# Revit family: BTicino-Hotel_UX_ONE-Thermostat
name_source: partatom
category: Equipement électrique
units: mm (PartAtom-declared; Revit-internal decimal feet)

## family parameters
Configuration du panneau = Deux colonnes, circuits au sein
Cote de connecteur circulaire = Utiliser le diamètre
Couper avec des vides une fois chargée = Non
Hôte = Face
Partagée = Non
Point de calcul de pièce = Non
Type d'élément = Tableau de raccordement

## types (8) — shared parameters
Avec affichage = Oui
Conditions Générale d'Utilisation = https://export.legrand.com
Ecran Tactile = Oui
Elévation par défaut = 1500 mm  [stored 4.92126 ft]
Fabricant = BTICINO
Fonction ne pas Déranger = Non
Fonctionnement en parallèle possible = Oui
Hauteur = 93 mm  [stored 0.305118 ft]
IK = 04
IP = 20
Largeur = 129 mm  [stored 0.423228 ft]
Matière = Plastique
Réglage manuel de la valeur de consigne = Oui
Site web configurateur = https://uxforhotels.legrand.com
Système de bus radio = Oui
profondeur d'encastrement = 50 mm  [stored 0.164042 ft]

## per-type parameters (varying)
| type | Couleur | Désignation produit | Hauteur pictogrammes | Hauteur vide | Matériau plaque | Matériau écran | Mode de pose | Plaque apparente | Plaque encastrée | Profondeur | Référence / Modèle | Tension |
| Noir 230V Encastré | Noir | HOTEL THERMOSTAT  ENCASTRE NOIR 230V | 0 mm  [stored 0 ft] | -40 mm  [stored -0.131234 ft] | LEGRAND_BLACK_PLASTIC | LEGRAND_BLACK_SCREEN | Encastré | Non | Oui | 52 mm | BT-465001 | 230 V AC |
| Noir 230V Apparent | Noir | HOTEL THERMOSTAT  SAILLIE NOIR 230V | 16 mm | 0 mm  [stored 0 ft] | LEGRAND_BLACK_PLASTIC | LEGRAND_BLACK_SCREEN | saillie | Oui | Non | 28 mm  [stored 0.0918635 ft] | BT-465002 | 230 V AC |
| Blanc 230V Encastré | Blanc | HOTEL THERMOSTAT  ENCASTRE BLANC 230V | 0 mm  [stored 0 ft] | -40 mm  [stored -0.131234 ft] | LEGRAND_WHITE_PLASTIC | LEGRAND_WHITE_SCREEN | Encastré | Non | Oui | 52 mm | BT-465003 | 230 V AC |
| Blanc 230V Apparent | Blanc | HOTEL THERMOSTAT  SAILLIE BLANC 230V | 16 mm | 0 mm  [stored 0 ft] | LEGRAND_WHITE_PLASTIC | LEGRAND_WHITE_SCREEN | saillie | Oui | Non | 28 mm  [stored 0.0918635 ft] | BT-465004 | 230 V AC |
| Noir 24V Encastré | Noir | HOTEL THERMOSTAT  ENCASTRE NOIR 24V | 0 mm  [stored 0 ft] | -40 mm  [stored -0.131234 ft] | LEGRAND_BLACK_PLASTIC | LEGRAND_BLACK_SCREEN | Encastré | Non | Oui | 52 mm | BT-465005 | 24 V |
| Noir 24V Apparent | Noir | HOTEL THERMOSTAT  SAILLIE NOIR 24V | 16 mm | 0 mm  [stored 0 ft] | LEGRAND_BLACK_PLASTIC | LEGRAND_BLACK_SCREEN | saillie | Oui | Non | 28 mm  [stored 0.0918635 ft] | BT-465006 | 24 V |
| Blanc 24V Encastré | Blanc | HOTEL THERMOSTAT ENCASTRE BLANC 24V | 0 mm  [stored 0 ft] | -40 mm  [stored -0.131234 ft] | LEGRAND_WHITE_PLASTIC | LEGRAND_WHITE_SCREEN | Encastré | Non | Oui | 52 mm | BT-465007 | 24 V |
| Blanc 24V Apparent | Blanc | HOTEL THERMOSTAT  SAILLIE BLANC 24V | 16 mm | 0 mm  [stored 0 ft] | LEGRAND_WHITE_PLASTIC | LEGRAND_WHITE_SCREEN | saillie | Oui | Non | 28 mm  [stored 0.0918635 ft] | BT-465008 | 24 V |

note: [stored X ft] marks values corroborated as IEEE doubles in the binary element streams (Revit-internal decimal feet)
